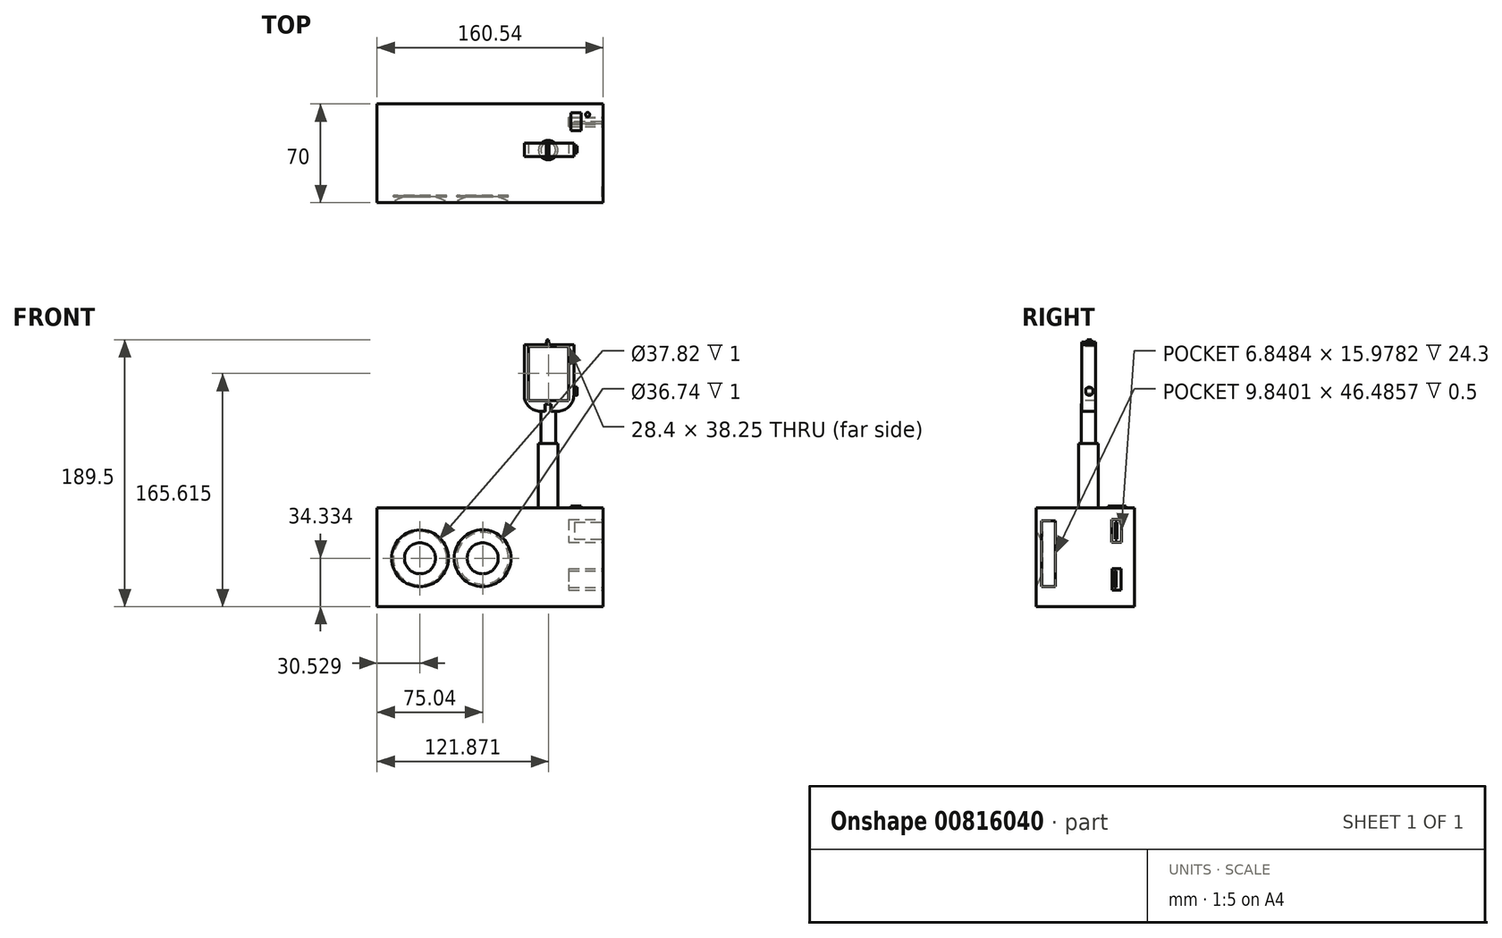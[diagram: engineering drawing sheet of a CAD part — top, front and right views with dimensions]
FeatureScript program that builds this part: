
annotation { "Feature Type Name" : "Feature", "Feature Type Description" : "" }
export const myFeature = defineFeature(function(context is Context, id is Id, definition is map)
    precondition{}
    {
        {
            var Q0;
            Q0=qCreatedBy(makeId("Top.planeOp"),FACE);
            var sketch = newSketch(context, id + "F0", { "sketchPlane" : qUnion([Q0])});
            skLineSegment(sketch, "E0.bottom", {"start": v(-75.04, 25.01) * mm, "end": v(85.5, 25.01) * mm});
            skLineSegment(sketch, "E0.top", {"start": v(-75.04, -44.99) * mm, "end": v(85.5, -44.99) * mm});
            skLineSegment(sketch, "E0.left", {"start": v(-75.04, 25.01) * mm, "end": v(-75.04, -44.99) * mm});
            skLineSegment(sketch, "E0.right", {"start": v(85.5, 25.01) * mm, "end": v(85.5, -44.99) * mm});
            skSolve(sketch);
        }
        {
            var Q0;
            Q0=makeQuery(id+"F0.imprint","IMPRINT",FACE,{"disambiguationData":[TD([[makeQuery(id+"F0.imprint","IMPRINT",EDGE,{"derivedFrom":sQuery(id+"F0.wireOp",EDGE,"E0.bottom")}),-1.0]])]});
            extrude(context, id + "F1", {"entities" : qUnion([Q0]), "depth" : 70 * mm, "offsetDistance" : 25 * mm});
        }
        {
            var Q0;
            Q0=makeQuery(id+"F1.opExtrude","SWEPT_FACE",FACE,{"disambiguationData":[OSD([sQuery(id+"F0.wireOp",EDGE,"E0.top")])]});
            var sketch = newSketch(context, id + "F2", { "sketchPlane" : qUnion([Q0])});
            skCircle(sketch, "E1", {"center": v(-44.51, 34.33) * mm, "radius": 20.16 * mm});
            skCircle(sketch, "E2", {"center": v(0, 34.33) * mm, "radius": 20.17 * mm});
            skSolve(sketch);
        }
        {
            var Q0;
            Q0=makeQuery(id+"F2.imprint","IMPRINT",FACE,{"disambiguationData":[TD([[makeQuery(id+"F2.imprint","IMPRINT",EDGE,{"derivedFrom":sQuery(id+"F2.wireOp",EDGE,"E2")}),1.0]])]});
            var Q1;
            Q1=makeQuery(id+"F2.imprint","IMPRINT",FACE,{"disambiguationData":[TD([[makeQuery(id+"F2.imprint","IMPRINT",EDGE,{"derivedFrom":sQuery(id+"F2.wireOp",EDGE,"E1")}),1.0]])]});
            extrude(context, id + "F3", {"entities" : qUnion([Q0, Q1]), "operationType" : NewBodyOperationType.REMOVE, "oppositeDirection" : true, "depth" : 5 * mm, "offsetDistance" : 25 * mm});
        }
        {
            var Q0;
            Q0=makeQuery(id+"F3.boolean.opBoolean","COPY",FACE,{"derivedFrom":makeQuery(id+"F3.opExtrude","CAP_FACE",FACE,{"disambiguationData":[OSD([sQuery(id+"F2.wireOp",EDGE,"E1")])],"isStart":false})});
            var sketch = newSketch(context, id + "F4", { "sketchPlane" : qUnion([Q0])});
            skCircle(sketch, "E3", {"center": v(-44.51, 34.33) * mm, "radius": 18.9 * mm});
            skCircle(sketch, "E4", {"center": v(0, 34.33) * mm, "radius": 18.37 * mm});
            skSolve(sketch);
        }
        {
            var Q0;
            Q0=makeQuery(id+"F3.boolean.opBoolean","COPY",FACE,{"derivedFrom":makeQuery(id+"F3.opExtrude","CAP_FACE",FACE,{"disambiguationData":[OSD([sQuery(id+"F2.wireOp",EDGE,"E1")])],"isStart":false})});
            var Q1;
            Q1=makeQuery(id+"F3.boolean.opBoolean","COPY",FACE,{"derivedFrom":makeQuery(id+"F3.opExtrude","CAP_FACE",FACE,{"disambiguationData":[OSD([sQuery(id+"F2.wireOp",EDGE,"E2")])],"isStart":false})});
            fillet(context, id + "F5", {"entities" : qUnion([Q0, Q1]), "radius" : 31.38 * mm, "tangentPropagation" : true, "allowEdgeOverflow" : false});
        }
        {
            var Q0;
            Q0=makeQuery(id+"F4.imprint","IMPRINT",FACE,{"disambiguationData":[TD([[makeQuery(id+"F4.imprint","IMPRINT",EDGE,{"derivedFrom":sQuery(id+"F4.wireOp",EDGE,"E3")}),1.0]])]});
            var Q1;
            Q1=makeQuery(id+"F4.imprint","IMPRINT",FACE,{"disambiguationData":[TD([[makeQuery(id+"F4.imprint","IMPRINT",EDGE,{"derivedFrom":sQuery(id+"F4.wireOp",EDGE,"E4")}),1.0]])]});
            extrude(context, id + "F6", {"entities" : qUnion([Q0, Q1]), "operationType" : NewBodyOperationType.REMOVE, "depth" : 1 * mm, "offsetDistance" : 25 * mm});
        }
        {
            var Q0;
            Q0=makeQuery(id+"F1.opExtrude","CAP_FACE",FACE,{"disambiguationData":[OSD([sQuery(id+"F0.wireOp",EDGE,"E0.bottom"),sQuery(id+"F0.wireOp",EDGE,"E0.top"),sQuery(id+"F0.wireOp",EDGE,"E0.left"),sQuery(id+"F0.wireOp",EDGE,"E0.right")])],"isStart":false});
            var sketch = newSketch(context, id + "F7", { "sketchPlane" : qUnion([Q0])});
            skLineSegment(sketch, "E5.bottom", {"start": v(-70.7, 20.82) * mm, "end": v(29.6, 20.82) * mm});
            skLineSegment(sketch, "E5.top", {"start": v(-70.7, -39.97) * mm, "end": v(29.6, -39.97) * mm});
            skLineSegment(sketch, "E5.left", {"start": v(-70.7, 20.82) * mm, "end": v(-70.7, -39.97) * mm});
            skLineSegment(sketch, "E5.right", {"start": v(29.6, 20.82) * mm, "end": v(29.6, -39.97) * mm});
            skLineSegment(sketch, "E6", {"start": v(-61, 20.82) * mm, "end": v(-61, -39.97) * mm});
            skLineSegment(sketch, "E7", {"start": v(-61, -39.97) * mm, "end": v(-50.43, -39.97) * mm});
            skLineSegment(sketch, "E8", {"start": v(-50.43, -39.97) * mm, "end": v(-50.43, 20.82) * mm});
            skLineSegment(sketch, "E9", {"start": v(-50.43, 20.82) * mm, "end": v(-39.6, 20.82) * mm});
            skLineSegment(sketch, "E10", {"start": v(-39.6, 20.82) * mm, "end": v(-39.6, -39.97) * mm});
            skLineSegment(sketch, "E11", {"start": v(-39.6, -39.97) * mm, "end": v(-29.48, -39.97) * mm});
            skLineSegment(sketch, "E12", {"start": v(-29.48, -39.97) * mm, "end": v(-29.48, 20.82) * mm});
            skLineSegment(sketch, "E13", {"start": v(-29.48, 20.82) * mm, "end": v(-18.59, 20.82) * mm});
            skLineSegment(sketch, "E14", {"start": v(-18.59, 20.82) * mm, "end": v(-18.59, -39.97) * mm});
            skLineSegment(sketch, "E15", {"start": v(-18.59, -39.97) * mm, "end": v(-8.15, -39.97) * mm});
            skLineSegment(sketch, "E16", {"start": v(-8.15, -39.97) * mm, "end": v(-8.15, 20.82) * mm});
            skLineSegment(sketch, "E17", {"start": v(-8.15, 20.82) * mm, "end": v(2.37, 20.82) * mm});
            skLineSegment(sketch, "E18", {"start": v(2.37, 20.82) * mm, "end": v(2.37, -39.97) * mm});
            skLineSegment(sketch, "E19", {"start": v(2.37, -39.97) * mm, "end": v(12.44, -39.97) * mm});
            skLineSegment(sketch, "E20", {"start": v(12.44, -39.97) * mm, "end": v(12.44, 20.82) * mm});
            skLineSegment(sketch, "E21", {"start": v(22.13, 20.82) * mm, "end": v(22.13, -39.97) * mm});
            skSolve(sketch);
        }
        {
            var Q0;
            {var subQ5=sQuery(id+"F7.wireOp",EDGE,"E5.left");Q0=makeQuery(id+"F7.imprint","IMPRINT",FACE,{"disambiguationData":[TD([[makeQuery(id+"F7.imprint","IMPRINT",EDGE,{"derivedFrom":subQ5}),-1.0]])]});}
            var sketch = newSketch(context, id + "F8", { "sketchPlane" : qUnion([Q0])});
            skLineSegment(sketch, "E22.bottom", {"start": v(62.82, 18.93) * mm, "end": v(69.88, 18.93) * mm});
            skLineSegment(sketch, "E22.top", {"start": v(62.82, 6.19) * mm, "end": v(69.88, 6.19) * mm});
            skLineSegment(sketch, "E22.left", {"start": v(62.82, 18.93) * mm, "end": v(62.82, 6.19) * mm});
            skLineSegment(sketch, "E22.right", {"start": v(69.88, 18.93) * mm, "end": v(69.88, 6.19) * mm});
            skSolve(sketch);
        }
        {
            var Q0;
            Q0=makeQuery(id+"F8.imprint","IMPRINT",FACE,{"disambiguationData":[TD([[makeQuery(id+"F8.imprint","IMPRINT",EDGE,{"derivedFrom":sQuery(id+"F8.wireOp",EDGE,"E22.bottom")}),1.0]])]});
            var sketch = newSketch(context, id + "F9", { "sketchPlane" : qUnion([Q0])});
            skCircle(sketch, "E23", {"center": v(74.57, 17.48) * mm, "radius": 1.5 * mm});
            skSolve(sketch);
        }
        {
            var Q0;
            Q0=makeQuery(id+"F9.imprint","IMPRINT",FACE,{"disambiguationData":[TD([[makeQuery(id+"F9.imprint","IMPRINT",EDGE,{"derivedFrom":makeQuery(id+"F8.imprint","IMPRINT",EDGE,{"derivedFrom":sQuery(id+"F8.wireOp",EDGE,"E22.bottom")})}),-1.0]])]});
            extrude(context, id + "F10", {"entities" : qUnion([Q0]), "operationType" : NewBodyOperationType.ADD, "depth" : 1.5 * mm, "offsetDistance" : 25 * mm});
        }
        {
            var Q0;
            Q0 = qSketchRegion(id + "F9", true);
            extrude(context, id + "F11", {"entities" : qUnion([Q0]), "operationType" : NewBodyOperationType.ADD, "depth" : 0.1 * mm, "offsetDistance" : 25 * mm});
        }
        {
            var Q0;
            Q0=makeQuery(id+"F1.opExtrude","SWEPT_FACE",FACE,{"disambiguationData":[OSD([sQuery(id+"F0.wireOp",EDGE,"E0.right")])]});
            var sketch = newSketch(context, id + "F12", { "sketchPlane" : qUnion([Q0])});
            skLineSegment(sketch, "E24.bottom", {"start": v(6.37, 64.77) * mm, "end": v(18.36, 64.77) * mm});
            skLineSegment(sketch, "E24.top", {"start": v(6.37, 8.27) * mm, "end": v(18.36, 8.27) * mm});
            skLineSegment(sketch, "E24.left", {"start": v(6.37, 64.77) * mm, "end": v(6.37, 8.27) * mm});
            skLineSegment(sketch, "E24.right", {"start": v(18.36, 64.77) * mm, "end": v(18.36, 8.27) * mm});
            skSolve(sketch);
        }
        {
            var Q0;
            Q0=makeQuery(id+"F12.imprint","IMPRINT",FACE,{"disambiguationData":[TD([[makeQuery(id+"F12.imprint","IMPRINT",EDGE,{"derivedFrom":sQuery(id+"F12.wireOp",EDGE,"E24.bottom")}),-1.0]])]});
            var sketch = newSketch(context, id + "F13", { "sketchPlane" : qUnion([Q0])});
            skLineSegment(sketch, "E25.bottom", {"start": v(8.84, 61.73) * mm, "end": v(15.7, 61.73) * mm});
            skLineSegment(sketch, "E25.top", {"start": v(8.84, 45.75) * mm, "end": v(15.7, 45.75) * mm});
            skLineSegment(sketch, "E25.left", {"start": v(8.84, 61.73) * mm, "end": v(8.84, 45.75) * mm});
            skLineSegment(sketch, "E25.right", {"start": v(15.7, 61.73) * mm, "end": v(15.7, 45.75) * mm});
            skSolve(sketch);
        }
        {
            var Q0;
            Q0=makeQuery(id+"F12.imprint","IMPRINT",FACE,{"disambiguationData":[TD([[makeQuery(id+"F12.imprint","IMPRINT",EDGE,{"derivedFrom":sQuery(id+"F12.wireOp",EDGE,"E24.bottom")}),-1.0]])]});
            var sketch = newSketch(context, id + "F14", { "sketchPlane" : qUnion([Q0])});
            skLineSegment(sketch, "E26.bottom", {"start": v(9.06, 26.95) * mm, "end": v(15.44, 26.95) * mm});
            skLineSegment(sketch, "E26.top", {"start": v(9.06, 11.84) * mm, "end": v(15.44, 11.84) * mm});
            skLineSegment(sketch, "E26.left", {"start": v(9.06, 26.95) * mm, "end": v(9.06, 11.84) * mm});
            skLineSegment(sketch, "E26.right", {"start": v(15.44, 26.95) * mm, "end": v(15.44, 11.84) * mm});
            skSolve(sketch);
        }
        {
            var Q0;
            Q0 = qSketchRegion(id + "F13", true);
            var Q1;
            Q1 = qSketchRegion(id + "F14", true);
            extrude(context, id + "F15", {"entities" : qUnion([Q0, Q1]), "operationType" : NewBodyOperationType.REMOVE, "oppositeDirection" : true, "depth" : 24.3 * mm, "offsetDistance" : 25 * mm});
        }
        {
            var Q0;
            Q0=makeQuery(id+"F12.imprint","IMPRINT",FACE,{"disambiguationData":[TD([[makeQuery(id+"F12.imprint","IMPRINT",EDGE,{"derivedFrom":sQuery(id+"F12.wireOp",EDGE,"E24.bottom")}),-1.0]])]});
            var sketch = newSketch(context, id + "F16", { "sketchPlane" : qUnion([Q0])});
            skLineSegment(sketch, "E27.bottom", {"start": v(11.35, 60.07) * mm, "end": v(12.68, 60.07) * mm});
            skLineSegment(sketch, "E27.top", {"start": v(11.35, 47.94) * mm, "end": v(12.68, 47.94) * mm});
            skLineSegment(sketch, "E27.left", {"start": v(11.35, 60.07) * mm, "end": v(11.35, 47.94) * mm});
            skLineSegment(sketch, "E27.right", {"start": v(12.68, 60.07) * mm, "end": v(12.68, 47.94) * mm});
            skLineSegment(sketch, "E28.bottom", {"start": v(11.41, 25.4) * mm, "end": v(12.68, 25.4) * mm});
            skLineSegment(sketch, "E28.top", {"start": v(11.41, 13.33) * mm, "end": v(12.68, 13.33) * mm});
            skLineSegment(sketch, "E28.left", {"start": v(11.41, 25.4) * mm, "end": v(11.41, 13.33) * mm});
            skLineSegment(sketch, "E28.right", {"start": v(12.68, 25.4) * mm, "end": v(12.68, 13.33) * mm});
            skSolve(sketch);
        }
        {
            var Q0;
            Q0=makeQuery(id+"F16.imprint","IMPRINT",FACE,{"disambiguationData":[TD([[makeQuery(id+"F16.imprint","IMPRINT",EDGE,{"derivedFrom":sQuery(id+"F16.wireOp",EDGE,"E27.bottom")}),-1.0]])]});
            extrude(context, id + "F17", {"entities" : qUnion([Q0]), "oppositeDirection" : true, "depth" : 20.2 * mm, "offsetDistance" : 25 * mm});
        }
        {
            var Q0;
            Q0=makeQuery(id+"F12.imprint","IMPRINT",FACE,{"disambiguationData":[TD([[makeQuery(id+"F12.imprint","IMPRINT",EDGE,{"derivedFrom":sQuery(id+"F12.wireOp",EDGE,"E24.bottom")}),-1.0]])]});
            var sketch = newSketch(context, id + "F18", { "sketchPlane" : qUnion([Q0])});
            skLineSegment(sketch, "E29.bottom", {"start": v(10.54, 25.24) * mm, "end": v(11.96, 25.24) * mm});
            skLineSegment(sketch, "E29.top", {"start": v(10.54, 13.48) * mm, "end": v(11.96, 13.48) * mm});
            skLineSegment(sketch, "E29.left", {"start": v(10.54, 25.24) * mm, "end": v(10.54, 13.48) * mm});
            skLineSegment(sketch, "E29.right", {"start": v(11.96, 25.24) * mm, "end": v(11.96, 13.48) * mm});
            skSolve(sketch);
        }
        {
            var Q0;
            Q0=makeQuery(id+"F18.imprint","IMPRINT",FACE,{"disambiguationData":[TD([[makeQuery(id+"F18.imprint","IMPRINT",EDGE,{"derivedFrom":sQuery(id+"F18.wireOp",EDGE,"E29.bottom")}),-1.0]])]});
            extrude(context, id + "F19", {"entities" : qUnion([Q0]), "operationType" : NewBodyOperationType.ADD, "oppositeDirection" : true, "depth" : 66.3 * mm, "offsetDistance" : 25 * mm});
        }
        {
            var Q0;
            Q0=makeQuery(id+"F12.imprint","IMPRINT",FACE,{"disambiguationData":[TD([[makeQuery(id+"F12.imprint","IMPRINT",EDGE,{"derivedFrom":sQuery(id+"F12.wireOp",EDGE,"E24.bottom")}),1.0]])]});
            var sketch = newSketch(context, id + "F20", { "sketchPlane" : qUnion([Q0])});
            skLineSegment(sketch, "E30.bottom", {"start": v(-40.98, 60.82) * mm, "end": v(-31.14, 60.82) * mm});
            skLineSegment(sketch, "E30.top", {"start": v(-40.98, 14.33) * mm, "end": v(-31.14, 14.33) * mm});
            skLineSegment(sketch, "E30.left", {"start": v(-40.98, 60.82) * mm, "end": v(-40.98, 14.33) * mm});
            skLineSegment(sketch, "E30.right", {"start": v(-31.14, 60.82) * mm, "end": v(-31.14, 14.33) * mm});
            skSolve(sketch);
        }
        {
            var Q0;
            Q0=makeQuery(id+"F20.imprint","IMPRINT",FACE,{"disambiguationData":[TD([[makeQuery(id+"F20.imprint","IMPRINT",EDGE,{"derivedFrom":sQuery(id+"F20.wireOp",EDGE,"E30.bottom")}),-1.0]])]});
            extrude(context, id + "F21", {"entities" : qUnion([Q0]), "operationType" : NewBodyOperationType.REMOVE, "oppositeDirection" : true, "depth" : 0.5 * mm, "offsetDistance" : 25 * mm});
        }
        {
            var Q0;
            Q0=makeQuery(id+"F8.imprint","IMPRINT",FACE,{"disambiguationData":[TD([[makeQuery(id+"F8.imprint","IMPRINT",EDGE,{"derivedFrom":sQuery(id+"F8.wireOp",EDGE,"E22.bottom")}),1.0]])]});
            var sketch = newSketch(context, id + "F22", { "sketchPlane" : qUnion([Q0])});
            skCircle(sketch, "E31", {"center": v(46.53, -7.75) * mm, "radius": 6.87 * mm});
            skSolve(sketch);
        }
        {
            var Q0;
            Q0=makeQuery(id+"F22.imprint","IMPRINT",FACE,{"disambiguationData":[TD([[makeQuery(id+"F22.imprint","IMPRINT",EDGE,{"derivedFrom":sQuery(id+"F22.wireOp",EDGE,"E31")}),1.0]])]});
            extrude(context, id + "F23", {"entities" : qUnion([Q0]), "operationType" : NewBodyOperationType.ADD, "depth" : 45.7 * mm, "offsetDistance" : 25 * mm});
        }
        {
            var Q0;
            Q0=makeQuery(id+"F23.opExtrude","CAP_FACE",FACE,{"disambiguationData":[OSD([sQuery(id+"F22.wireOp",EDGE,"E31")])],"isStart":false});
            var sketch = newSketch(context, id + "F24", { "sketchPlane" : qUnion([Q0])});
            skCircle(sketch, "E32", {"center": v(46.53, -7.75) * mm, "radius": 5.23 * mm});
            skSolve(sketch);
        }
        {
            var Q0;
            Q0=makeQuery(id+"F24.imprint","IMPRINT",FACE,{"disambiguationData":[TD([[makeQuery(id+"F24.imprint","IMPRINT",EDGE,{"derivedFrom":sQuery(id+"F24.wireOp",EDGE,"E32")}),1.0]])]});
            extrude(context, id + "F25", {"entities" : qUnion([Q0]), "operationType" : NewBodyOperationType.ADD, "depth" : 28.1 * mm, "offsetDistance" : 25 * mm});
        }
        {
            var Q0;
            Q0=makeQuery(id+"F25.opExtrude","CAP_FACE",FACE,{"disambiguationData":[OSD([sQuery(id+"F24.wireOp",EDGE,"E32")])],"isStart":false});
            var sketch = newSketch(context, id + "F26", { "sketchPlane" : qUnion([Q0])});
            skLineSegment(sketch, "E33.bottom", {"start": v(29.5, -2.64) * mm, "end": v(64.75, -2.64) * mm});
            skLineSegment(sketch, "E33.top", {"start": v(29.5, -12.45) * mm, "end": v(64.75, -12.45) * mm});
            skLineSegment(sketch, "E33.left", {"start": v(29.5, -2.64) * mm, "end": v(29.5, -12.45) * mm});
            skLineSegment(sketch, "E33.right", {"start": v(64.75, -2.64) * mm, "end": v(64.75, -12.45) * mm});
            skSolve(sketch);
        }
        {
            var Q0;
            {var subQ0=sQuery(id+"F26.wireOp",EDGE,"E33.right");Q0=makeQuery(id+"F26.imprint","IMPRINT",FACE,{"disambiguationData":[TD([[makeQuery(id+"F26.imprint","IMPRINT",EDGE,{"derivedFrom":subQ0}),-1.0]])]});}
            var Q1;
            {var subQ0=sQuery(id+"F26.wireOp",EDGE,"E33.left");Q1=makeQuery(id+"F26.imprint","IMPRINT",FACE,{"disambiguationData":[TD([[makeQuery(id+"F26.imprint","IMPRINT",EDGE,{"derivedFrom":subQ0}),1.0]])]});}
            var Q2;
            {var subQ0=sQuery(id+"F26.wireOp",EDGE,"E33.bottom");var subQ1=makeQuery(id+"F25.opExtrude","CAP_EDGE",EDGE,{"disambiguationData":[OSD([sQuery(id+"F24.wireOp",EDGE,"E32")])],"isStart":false});var subQ2=makeQuery(id+"F26.imprint","INTERSECT",VERTEX,{"disambiguationData":[OD(0.0)],"derivedFrom":[subQ1,subQ0]});Q2=makeQuery(id+"F26.imprint","IMPRINT",FACE,{"disambiguationData":[TD([[makeQuery(id+"F26.imprint","IMPRINT",EDGE,{"disambiguationData":[TD([[subQ2,-1.0]])],"derivedFrom":subQ0}),-1.0]])]});}
            extrude(context, id + "F27", {"entities" : qUnion([Q0, Q1, Q2]), "operationType" : NewBodyOperationType.ADD, "depth" : 42.3 * mm, "offsetDistance" : 25 * mm});
        }
        {
            var Q0;
            Q0=makeQuery(id+"F27.opExtrude","SWEPT_FACE",FACE,{"disambiguationData":[OSD([sQuery(id+"F26.wireOp",EDGE,"E33.top")])]});
            var sketch = newSketch(context, id + "F28", { "sketchPlane" : qUnion([Q0])});
            skLineSegment(sketch, "E34.bottom", {"start": v(32.63, 184.74) * mm, "end": v(61.03, 184.74) * mm});
            skLineSegment(sketch, "E34.top", {"start": v(32.63, 146.5) * mm, "end": v(61.03, 146.5) * mm});
            skLineSegment(sketch, "E34.left", {"start": v(32.63, 184.74) * mm, "end": v(32.63, 146.5) * mm});
            skLineSegment(sketch, "E34.right", {"start": v(61.03, 184.74) * mm, "end": v(61.03, 146.5) * mm});
            skSolve(sketch);
        }
        {
            var Q0;
            Q0=makeQuery(id+"F28.imprint","IMPRINT",FACE,{"disambiguationData":[TD([[makeQuery(id+"F28.imprint","IMPRINT",EDGE,{"derivedFrom":sQuery(id+"F28.wireOp",EDGE,"E34.bottom")}),-1.0]])]});
            extrude(context, id + "F29", {"entities" : qUnion([Q0]), "operationType" : NewBodyOperationType.REMOVE, "oppositeDirection" : true, "depth" : 39.1 * mm, "offsetDistance" : 25 * mm});
        }
        {
            var Q0;
            {var subQ0=sQuery(id+"F26.wireOp",EDGE,"E33.bottom");var subQ1=sQuery(id+"F26.wireOp",EDGE,"E33.top");var subQ3=sQuery(id+"F26.wireOp",EDGE,"E33.left");Q0=makeQuery(id+"F27.boolean.opBoolean","SPLIT",FACE,{"disambiguationData":[TD([makeQuery(id+"F27.opExtrude","SWEPT_FACE",FACE,{"disambiguationData":[OSD([subQ3])]})])],"derivedFrom":makeQuery(id+"F27.opExtrude","CAP_FACE",FACE,{"disambiguationData":[OSD([subQ0,subQ1,subQ3,sQuery(id+"F26.wireOp",EDGE,"E33.right")])],"isStart":true})});}
            var sketch = newSketch(context, id + "F30", { "sketchPlane" : qUnion([Q0])});
            skSolve(sketch);
        }
        {
            var Q0;
            {var subQ0=sQuery(id+"F26.wireOp",EDGE,"E33.bottom");var subQ1=sQuery(id+"F26.wireOp",EDGE,"E33.top");var subQ3=sQuery(id+"F26.wireOp",EDGE,"E33.right");Q0=makeQuery(id+"F27.boolean.opBoolean","SPLIT",FACE,{"disambiguationData":[TD([makeQuery(id+"F27.opExtrude","SWEPT_FACE",FACE,{"disambiguationData":[OSD([subQ3])]})])],"derivedFrom":makeQuery(id+"F27.opExtrude","CAP_FACE",FACE,{"disambiguationData":[OSD([subQ0,subQ1,sQuery(id+"F26.wireOp",EDGE,"E33.left"),subQ3])],"isStart":true})});}
            var Q1;
            {var subQ0=sQuery(id+"F26.wireOp",EDGE,"E33.left");Q1=makeQuery(id+"F30.imprint","IMPRINT",FACE,{"disambiguationData":[TD([[makeQuery(id+"F30.imprint","IMPRINT",EDGE,{"derivedFrom":makeQuery(id+"F27.opExtrude","CAP_EDGE",EDGE,{"disambiguationData":[OSD([subQ0])],"isStart":true})}),-1.0]])]});}
            extrude(context, id + "F31", {"entities" : qUnion([Q0, Q1]), "operationType" : NewBodyOperationType.ADD, "depth" : 5.1 * mm, "offsetDistance" : 25 * mm});
        }
        {
            var Q0;
            Q0=makeQuery(id+"F31.opExtrude","CAP_EDGE",EDGE,{"disambiguationData":[OSD([sQuery(id+"F26.wireOp",EDGE,"E33.right")])],"isStart":false});
            var Q1;
            Q1=makeQuery(id+"F31.opExtrude","CAP_EDGE",EDGE,{"disambiguationData":[OSD([sQuery(id+"F26.wireOp",EDGE,"E33.left")])],"isStart":false});
            fillet(context, id + "F32", {"entities" : qUnion([Q0, Q1]), "radius" : 11.6 * mm, "tangentPropagation" : true, "allowEdgeOverflow" : false});
        }
        {
            var Q0;
            {var subQ0=sQuery(id+"F26.wireOp",EDGE,"E33.right");Q0=makeQuery(id+"F31.boolean.opBoolean","MERGE",FACE,{"derivedFrom":[makeQuery(id+"F27.opExtrude","SWEPT_FACE",FACE,{"disambiguationData":[OSD([subQ0])]}),makeQuery(id+"F31.opExtrude","SWEPT_FACE",FACE,{"disambiguationData":[OSD([subQ0])]})]});}
            var sketch = newSketch(context, id + "F33", { "sketchPlane" : qUnion([Q0])});
            skLineSegment(sketch, "E35.bottom", {"start": v(-9.73, 155.02) * mm, "end": v(-4.61, 155.02) * mm});
            skLineSegment(sketch, "E35.top", {"start": v(-9.73, 151.64) * mm, "end": v(-4.61, 151.64) * mm});
            skLineSegment(sketch, "E35.left", {"start": v(-9.73, 155.02) * mm, "end": v(-9.73, 151.64) * mm});
            skLineSegment(sketch, "E35.right", {"start": v(-4.61, 155.02) * mm, "end": v(-4.61, 151.64) * mm});
            skSolve(sketch);
        }
        {
            var Q0;
            Q0=makeQuery(id+"F33.imprint","IMPRINT",FACE,{"disambiguationData":[TD([[makeQuery(id+"F33.imprint","IMPRINT",EDGE,{"derivedFrom":sQuery(id+"F33.wireOp",EDGE,"E35.bottom")}),-1.0]])]});
            extrude(context, id + "F34", {"entities" : qUnion([Q0]), "operationType" : NewBodyOperationType.ADD, "depth" : 1.3 * mm, "offsetDistance" : 25 * mm});
        }
        {
            var Q0;
            Q0=makeQuery(id+"F34.opExtrude","CAP_FACE",FACE,{"disambiguationData":[OSD([sQuery(id+"F33.wireOp",EDGE,"E35.bottom"),sQuery(id+"F33.wireOp",EDGE,"E35.top"),sQuery(id+"F33.wireOp",EDGE,"E35.left"),sQuery(id+"F33.wireOp",EDGE,"E35.right")])],"isStart":false});
            var sketch = newSketch(context, id + "F35", { "sketchPlane" : qUnion([Q0])});
            skCircle(sketch, "E36", {"center": v(-7.17, 152.97) * mm, "radius": 2.88 * mm});
            skPoint(sketch, "E36.centerSnap0", {"position": v(-7.17, 155.02) * mm});
            skSolve(sketch);
        }
        {
            var Q0;
            {var subQ0=sQuery(id+"F35.wireOp",EDGE,"E36");var subQ1=makeQuery(id+"F34.opExtrude","CAP_EDGE",EDGE,{"disambiguationData":[OSD([sQuery(id+"F33.wireOp",EDGE,"E35.bottom")])],"isStart":false});var subQ2=makeQuery(id+"F35.imprint","INTERSECT",VERTEX,{"disambiguationData":[OD(0.0)],"derivedFrom":[subQ1,subQ0]});Q0=makeQuery(id+"F35.imprint","IMPRINT",FACE,{"disambiguationData":[TD([[makeQuery(id+"F35.imprint","IMPRINT",EDGE,{"disambiguationData":[TD([[subQ2,-1.0]])],"derivedFrom":subQ0}),1.0]])]});}
            var Q1;
            {var subQ4=makeQuery(id+"F34.opExtrude","CAP_EDGE",EDGE,{"disambiguationData":[OSD([sQuery(id+"F33.wireOp",EDGE,"E35.top")])],"isStart":false});Q1=makeQuery(id+"F35.imprint","IMPRINT",FACE,{"disambiguationData":[TD([[makeQuery(id+"F35.imprint","IMPRINT",EDGE,{"derivedFrom":subQ4}),1.0]])]});}
            var Q2;
            {var subQ1=makeQuery(id+"F34.opExtrude","CAP_EDGE",EDGE,{"disambiguationData":[OSD([sQuery(id+"F33.wireOp",EDGE,"E35.top")])],"isStart":false});Q2=makeQuery(id+"F35.imprint","IMPRINT",FACE,{"disambiguationData":[TD([[makeQuery(id+"F35.imprint","IMPRINT",EDGE,{"derivedFrom":subQ1}),-1.0]])]});}
            extrude(context, id + "F36", {"entities" : qUnion([Q0, Q1, Q2]), "operationType" : NewBodyOperationType.ADD, "depth" : 1 * mm, "offsetDistance" : 25 * mm});
        }
        {
            var Q0;
            Q0=makeQuery(id+"F27.opExtrude","CAP_FACE",FACE,{"disambiguationData":[OSD([sQuery(id+"F26.wireOp",EDGE,"E33.bottom"),sQuery(id+"F26.wireOp",EDGE,"E33.top"),sQuery(id+"F26.wireOp",EDGE,"E33.left"),sQuery(id+"F26.wireOp",EDGE,"E33.right")])],"isStart":false});
            var sketch = newSketch(context, id + "F37", { "sketchPlane" : qUnion([Q0])});
            skLineSegment(sketch, "E37.bottom", {"start": v(45.26, -2.64) * mm, "end": v(47.12, -2.64) * mm});
            skLineSegment(sketch, "E37.top", {"start": v(45.26, -12.45) * mm, "end": v(47.12, -12.45) * mm});
            skLineSegment(sketch, "E37.left", {"start": v(45.26, -2.64) * mm, "end": v(45.26, -12.45) * mm});
            skLineSegment(sketch, "E37.right", {"start": v(47.12, -2.64) * mm, "end": v(47.12, -12.45) * mm});
            skSolve(sketch);
        }
        {
            var Q0;
            Q0=makeQuery(id+"F37.imprint","IMPRINT",FACE,{"disambiguationData":[TD([[makeQuery(id+"F37.imprint","IMPRINT",EDGE,{"derivedFrom":sQuery(id+"F37.wireOp",EDGE,"E37.bottom")}),-1.0]])]});
            extrude(context, id + "F38", {"entities" : qUnion([Q0]), "operationType" : NewBodyOperationType.ADD, "depth" : 1.7 * mm, "offsetDistance" : 25 * mm});
        }
        {
            var Q0;
            Q0=makeQuery(id+"F38.opExtrude","CAP_FACE",FACE,{"disambiguationData":[OSD([sQuery(id+"F37.wireOp",EDGE,"E37.bottom"),sQuery(id+"F37.wireOp",EDGE,"E37.top"),sQuery(id+"F37.wireOp",EDGE,"E37.left"),sQuery(id+"F37.wireOp",EDGE,"E37.right")])],"isStart":false});
            var sketch = newSketch(context, id + "F39", { "sketchPlane" : qUnion([Q0])});
            skEllipse(sketch, "E38", {"center": v(46.24, -7.1) * mm, "majorRadius": 1.7 * mm, "minorRadius": 0.67 * mm, "majorAxis": v(0, -1)});
            skSolve(sketch);
        }
        {
            var Q0;
            Q0=makeQuery(id+"F39.imprint","IMPRINT",FACE,{"disambiguationData":[TD([[makeQuery(id+"F39.imprint","IMPRINT",EDGE,{"derivedFrom":sQuery(id+"F39.wireOp",EDGE,"E38")}),1.0]])]});
            extrude(context, id + "F40", {"entities" : qUnion([Q0]), "operationType" : NewBodyOperationType.ADD, "depth" : 1.7 * mm, "offsetDistance" : 25 * mm});
        }
    });
